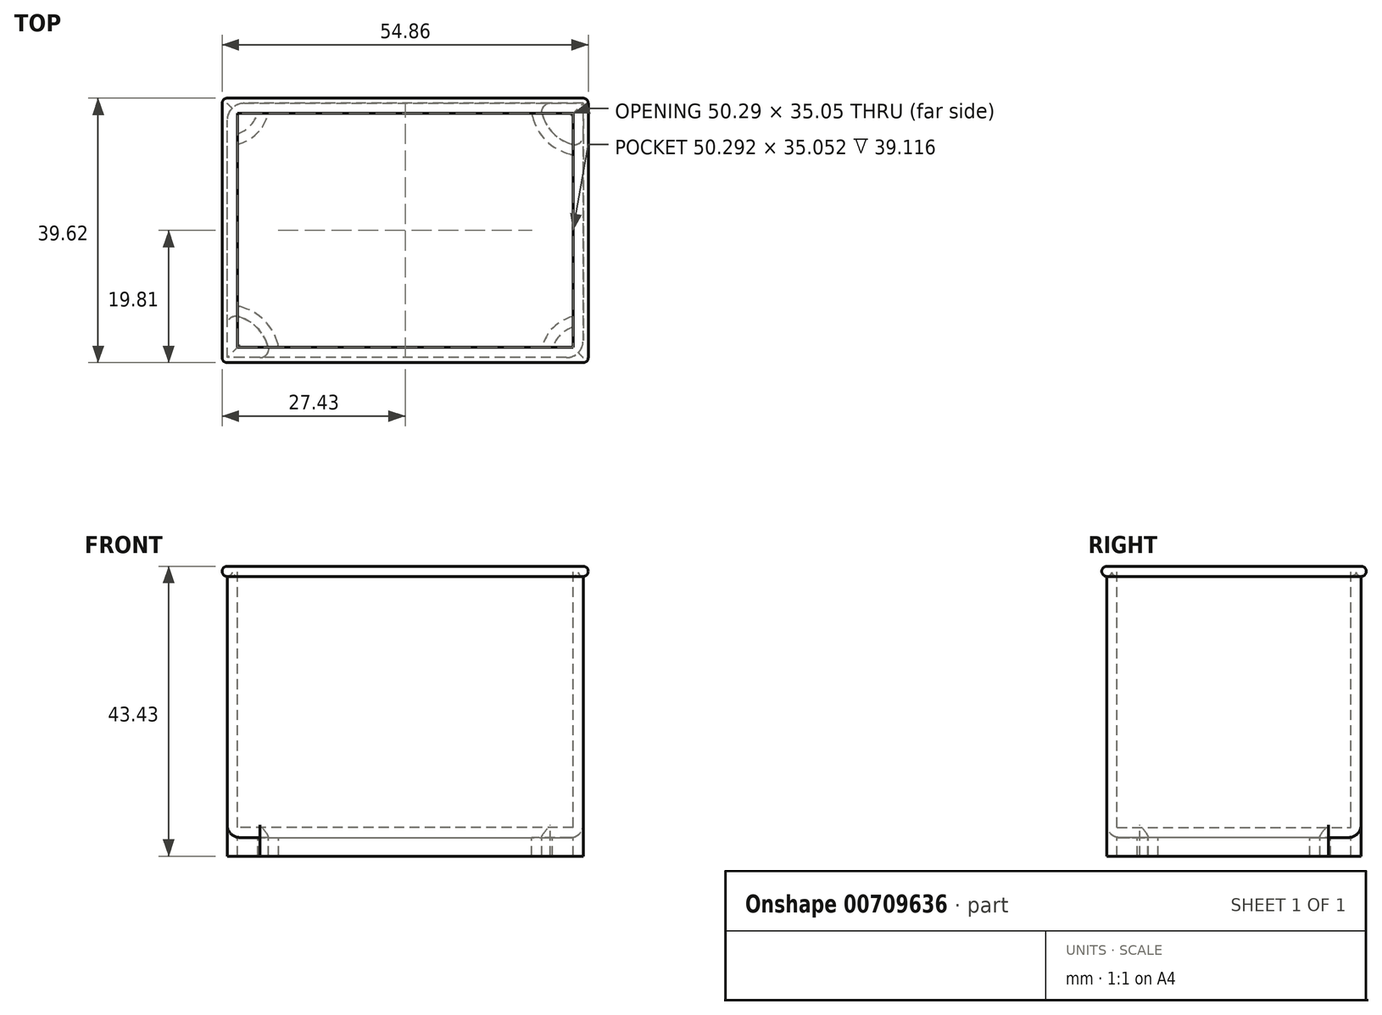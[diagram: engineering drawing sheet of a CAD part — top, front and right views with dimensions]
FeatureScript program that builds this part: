
annotation { "Feature Type Name" : "Feature", "Feature Type Description" : "" }
export const myFeature = defineFeature(function(context is Context, id is Id, definition is map)
    precondition{}
    {
        {
            var Q0;
            Q0=qCreatedBy(makeId("Front.planeOp"),FACE);
            var sketch = newSketch(context, id + "F0", { "sketchPlane" : qUnion([Q0])});
            skLineSegment(sketch, "E0.bottom", {"start": v(26.67, -20.32) * mm, "end": v(-26.67, -20.32) * mm});
            skLineSegment(sketch, "E0.top", {"start": v(26.67, 20.32) * mm, "end": v(-26.67, 20.32) * mm});
            skLineSegment(sketch, "E0.left", {"start": v(26.67, -20.32) * mm, "end": v(26.67, 20.32) * mm});
            skLineSegment(sketch, "E0.right", {"start": v(-26.67, -20.32) * mm, "end": v(-26.67, 20.32) * mm});
            skPoint(sketch, "E0.middle", {"position": v(0, 0) * mm});
            skSolve(sketch);
        }
        {
            var Q0;
            Q0=makeQuery(id+"F0.imprint","IMPRINT",FACE,{"disambiguationData":[TD([[makeQuery(id+"F0.imprint","IMPRINT",EDGE,{"derivedFrom":sQuery(id+"F0.wireOp",EDGE,"E0.bottom")}),-1.0]])]});
            extrude(context, id + "F1", {"entities" : qUnion([Q0]), "depth" : 38.1 * mm, "symmetric" : true});
        }
        {
            var Q0;
            Q0=makeQuery(id+"F1.opExtrude","SWEPT_FACE",FACE,{"disambiguationData":[OSD([sQuery(id+"F0.wireOp",EDGE,"E0.top")])]});
            shell(context, id + "F2", {"entities" : qUnion([Q0]), "thickness" : 1.52 * mm});
        }
        {
            var Q0;
            Q0=makeQuery(id+"F1.opExtrude","CAP_FACE",FACE,{"disambiguationData":[OSD([sQuery(id+"F0.wireOp",EDGE,"E0.bottom"),sQuery(id+"F0.wireOp",EDGE,"E0.top"),sQuery(id+"F0.wireOp",EDGE,"E0.left"),sQuery(id+"F0.wireOp",EDGE,"E0.right")])],"isStart":false});
            var sketch = newSketch(context, id + "F3", { "sketchPlane" : qUnion([Q0])});
            skArc(sketch, "E1", {"start": v(-26.67, 20.32) * mm, "mid": v(-27.43, 19.56) * mm, "end": v(-26.67, 18.8) * mm});
            skSolve(sketch);
        }
        {
            var Q0;
            {var subQ0=sQuery(id+"F3.wireOp",EDGE,"E1");Q0=makeQuery(id+"F3.imprint","IMPRINT",FACE,{"disambiguationData":[TD([[makeQuery(id+"F3.imprint","IMPRINT",EDGE,{"derivedFrom":subQ0}),1.0]])]});}
            var Q1;
            Q1=makeQuery(id+"F1.opExtrude","SWEPT_EDGE",EDGE,{"disambiguationData":[OSD([sQuery(id+"F0.wireOp",EDGE,"E0.top"),sQuery(id+"F0.wireOp",EDGE,"E0.right")])]});
            var Q2;
            Q2=makeQuery(id+"F1.opExtrude","CAP_EDGE",EDGE,{"disambiguationData":[OSD([sQuery(id+"F0.wireOp",EDGE,"E0.top")])],"isStart":true});
            var Q3;
            Q3=makeQuery(id+"F1.opExtrude","SWEPT_EDGE",EDGE,{"disambiguationData":[OSD([sQuery(id+"F0.wireOp",EDGE,"E0.top"),sQuery(id+"F0.wireOp",EDGE,"E0.left")])]});
            var Q4;
            Q4=makeQuery(id+"F1.opExtrude","CAP_EDGE",EDGE,{"disambiguationData":[OSD([sQuery(id+"F0.wireOp",EDGE,"E0.top")])],"isStart":false});
            sweep(context, id + "F4", {"operationType" : NewBodyOperationType.ADD, "profiles" : qUnion([Q0]), "path" : qUnion([Q1, Q2, Q3, Q4])});
        }
        {
            var Q0;
            Q0=makeQuery(id+"F1.opExtrude","SWEPT_FACE",FACE,{"disambiguationData":[OSD([sQuery(id+"F0.wireOp",EDGE,"E0.bottom")])]});
            var sketch = newSketch(context, id + "F5", { "sketchPlane" : qUnion([Q0])});
            skLineSegment(sketch, "E2.bottom", {"start": v(26.67, 19.05) * mm, "end": v(21.75, 19.05) * mm});
            skLineSegment(sketch, "E2.left", {"start": v(26.67, 19.05) * mm, "end": v(26.67, 14.13) * mm});
            skPoint(sketch, "E3.newPointA", {"position": v(20.32, 19.05) * mm});
            skArc(sketch, "E4", {"start": v(20.52, 17.46) * mm, "mid": v(22.18, 14.56) * mm, "end": v(25.08, 12.9) * mm});
            skArc(sketch, "E5.filletArc", {"start": v(21.75, 19.05) * mm, "mid": v(20.75, 18.56) * mm, "end": v(20.52, 17.46) * mm});
            skPoint(sketch, "E6.visualSharp", {"position": v(26.67, 12.7) * mm});
            skArc(sketch, "E6.filletArc", {"start": v(25.08, 12.9) * mm, "mid": v(26.18, 13.13) * mm, "end": v(26.67, 14.13) * mm});
            skArc(sketch, "E7.MirrorCS", {"start": v(-21.75, 19.05) * mm, "mid": v(-20.75, 18.56) * mm, "end": v(-20.52, 17.46) * mm});
            skArc(sketch, "E8.MirrorCS", {"start": v(-20.52, 17.46) * mm, "mid": v(-22.18, 14.56) * mm, "end": v(-25.08, 12.9) * mm});
            skArc(sketch, "E9.MirrorCS", {"start": v(-25.08, 12.9) * mm, "mid": v(-26.18, 13.13) * mm, "end": v(-26.67, 14.13) * mm});
            skLineSegment(sketch, "E10.MirrorCS", {"start": v(-26.67, 19.05) * mm, "end": v(-26.67, 14.13) * mm});
            skLineSegment(sketch, "E11.MirrorCS", {"start": v(-26.67, 19.05) * mm, "end": v(-21.75, 19.05) * mm});
            skArc(sketch, "E12.MirrorCS", {"start": v(-20.52, -17.46) * mm, "mid": v(-22.18, -14.56) * mm, "end": v(-25.08, -12.9) * mm});
            skArc(sketch, "E13.MirrorCS", {"start": v(-21.75, -19.05) * mm, "mid": v(-20.75, -18.56) * mm, "end": v(-20.52, -17.46) * mm});
            skLineSegment(sketch, "E14.MirrorCS", {"start": v(-26.67, -19.05) * mm, "end": v(-21.75, -19.05) * mm});
            skLineSegment(sketch, "E15.MirrorCS", {"start": v(-26.67, -19.05) * mm, "end": v(-26.67, -14.13) * mm});
            skArc(sketch, "E16.MirrorCS", {"start": v(-25.08, -12.9) * mm, "mid": v(-26.18, -13.13) * mm, "end": v(-26.67, -14.13) * mm});
            skArc(sketch, "E17.MirrorCS", {"start": v(21.75, -19.05) * mm, "mid": v(20.75, -18.56) * mm, "end": v(20.52, -17.46) * mm});
            skArc(sketch, "E18.MirrorCS", {"start": v(20.52, -17.46) * mm, "mid": v(22.18, -14.56) * mm, "end": v(25.08, -12.9) * mm});
            skArc(sketch, "E19.MirrorCS", {"start": v(25.08, -12.9) * mm, "mid": v(26.18, -13.13) * mm, "end": v(26.67, -14.13) * mm});
            skLineSegment(sketch, "E20.MirrorCS", {"start": v(26.67, -19.05) * mm, "end": v(26.67, -14.13) * mm});
            skLineSegment(sketch, "E21.MirrorCS", {"start": v(26.67, -19.05) * mm, "end": v(21.75, -19.05) * mm});
            skSolve(sketch);
        }
        {
            var Q0;
            Q0=makeQuery(id+"F5.imprint","IMPRINT",FACE,{"disambiguationData":[TD([[makeQuery(id+"F5.imprint","IMPRINT",EDGE,{"derivedFrom":sQuery(id+"F5.wireOp",EDGE,"E2.bottom")}),1.0]])]});
            var Q1;
            Q1=makeQuery(id+"F5.imprint","IMPRINT",FACE,{"disambiguationData":[TD([[makeQuery(id+"F5.imprint","IMPRINT",EDGE,{"derivedFrom":sQuery(id+"F5.wireOp",EDGE,"E8.MirrorCS")}),-1.0]])]});
            var Q2;
            Q2=makeQuery(id+"F5.imprint","IMPRINT",FACE,{"disambiguationData":[TD([[makeQuery(id+"F5.imprint","IMPRINT",EDGE,{"derivedFrom":sQuery(id+"F5.wireOp",EDGE,"E12.MirrorCS")}),1.0]])]});
            var Q3;
            Q3=makeQuery(id+"F5.imprint","IMPRINT",FACE,{"disambiguationData":[TD([[makeQuery(id+"F5.imprint","IMPRINT",EDGE,{"derivedFrom":sQuery(id+"F5.wireOp",EDGE,"E17.MirrorCS")}),-1.0]])]});
            extrude(context, id + "F6", {"entities" : qUnion([Q0, Q1, Q2, Q3]), "operationType" : NewBodyOperationType.ADD, "depth" : 2.8 * mm});
        }
        {
            var Q0;
            Q0=makeQuery(id+"F6.opExtrude","CAP_FACE",FACE,{"disambiguationData":[OSD([sQuery(id+"F5.wireOp",EDGE,"E2.bottom"),sQuery(id+"F5.wireOp",EDGE,"E2.left"),sQuery(id+"F5.wireOp",EDGE,"E4"),sQuery(id+"F5.wireOp",EDGE,"E5.filletArc"),sQuery(id+"F5.wireOp",EDGE,"E6.filletArc")])],"isStart":false});
            var Q1;
            Q1=makeQuery(id+"F6.opExtrude","CAP_FACE",FACE,{"disambiguationData":[OSD([sQuery(id+"F5.wireOp",EDGE,"E8.MirrorCS"),sQuery(id+"F5.wireOp",EDGE,"E9.MirrorCS"),sQuery(id+"F5.wireOp",EDGE,"E10.MirrorCS"),sQuery(id+"F5.wireOp",EDGE,"E7.MirrorCS"),sQuery(id+"F5.wireOp",EDGE,"E11.MirrorCS")])],"isStart":false});
            var Q2;
            Q2=makeQuery(id+"F6.opExtrude","CAP_FACE",FACE,{"disambiguationData":[OSD([sQuery(id+"F5.wireOp",EDGE,"E12.MirrorCS"),sQuery(id+"F5.wireOp",EDGE,"E13.MirrorCS"),sQuery(id+"F5.wireOp",EDGE,"E14.MirrorCS"),sQuery(id+"F5.wireOp",EDGE,"E15.MirrorCS"),sQuery(id+"F5.wireOp",EDGE,"E16.MirrorCS")])],"isStart":false});
            var Q3;
            Q3=makeQuery(id+"F6.opExtrude","CAP_FACE",FACE,{"disambiguationData":[OSD([sQuery(id+"F5.wireOp",EDGE,"E17.MirrorCS"),sQuery(id+"F5.wireOp",EDGE,"E18.MirrorCS"),sQuery(id+"F5.wireOp",EDGE,"E19.MirrorCS"),sQuery(id+"F5.wireOp",EDGE,"E20.MirrorCS"),sQuery(id+"F5.wireOp",EDGE,"E21.MirrorCS")])],"isStart":false});
            shell(context, id + "F7", {"entities" : qUnion([Q0, Q1, Q2, Q3]), "thickness" : 1.52 * mm});
        }
        {
            var Q0;
            Q0=makeQuery(id+"F1.opExtrude","SWEPT_EDGE",EDGE,{"disambiguationData":[OSD([sQuery(id+"F0.wireOp",EDGE,"E0.bottom"),sQuery(id+"F0.wireOp",EDGE,"E0.right")])]});
            var Q1;
            Q1=makeQuery(id+"F1.opExtrude","CAP_EDGE",EDGE,{"disambiguationData":[OSD([sQuery(id+"F0.wireOp",EDGE,"E0.bottom")])],"isStart":false});
            var Q2;
            Q2=makeQuery(id+"F1.opExtrude","SWEPT_EDGE",EDGE,{"disambiguationData":[OSD([sQuery(id+"F0.wireOp",EDGE,"E0.bottom"),sQuery(id+"F0.wireOp",EDGE,"E0.left")])]});
            var Q3;
            Q3=makeQuery(id+"F1.opExtrude","CAP_EDGE",EDGE,{"disambiguationData":[OSD([sQuery(id+"F0.wireOp",EDGE,"E0.bottom")])],"isStart":true});
            fillet(context, id + "F8", {"entities" : qUnion([Q0, Q1, Q2, Q3]), "radius" : 1.9 * mm, "tangentPropagation" : true, "allowEdgeOverflow" : false});
        }
        {
            var Q0;
            Q0=makeQuery(id+"F4.opSweep","MID_CAP_EDGE",EDGE,{"disambiguationData":[OSD([sQuery(id+"F0.wireOp",EDGE,"E0.top"),sQuery(id+"F0.wireOp",EDGE,"E0.left"),sQuery(id+"F3.wireOp",EDGE,"E1")])],"capPos":3.0});
            var Q1;
            Q1=makeQuery(id+"F4.opSweep","MID_CAP_EDGE",EDGE,{"disambiguationData":[OSD([sQuery(id+"F0.wireOp",EDGE,"E0.top"),sQuery(id+"F0.wireOp",EDGE,"E0.left"),sQuery(id+"F3.wireOp",EDGE,"E1")])],"capPos":2.0});
            var Q2;
            Q2=makeQuery(id+"F4.opSweep","MID_CAP_EDGE",EDGE,{"disambiguationData":[OSD([sQuery(id+"F0.wireOp",EDGE,"E0.top"),sQuery(id+"F0.wireOp",EDGE,"E0.right"),sQuery(id+"F3.wireOp",EDGE,"E1")])],"capPos":1.0});
            var Q3;
            Q3=makeQuery(id+"F4.opSweep","CAP_EDGE",EDGE,{"disambiguationData":[OSD([sQuery(id+"F0.wireOp",EDGE,"E0.top"),sQuery(id+"F0.wireOp",EDGE,"E0.right"),sQuery(id+"F3.wireOp",EDGE,"E1")])],"isStart":true});
            fillet(context, id + "F9", {"entities" : qUnion([Q0, Q1, Q2, Q3]), "radius" : 0.76 * mm, "tangentPropagation" : true, "allowEdgeOverflow" : false});
        }
        {
            var Q0;
            Q0=makeQuery(id+"F6.boolean.opBoolean","MERGE",EDGE,{"derivedFrom":[makeQuery(id+"F1.opExtrude","CAP_EDGE",EDGE,{"disambiguationData":[OSD([sQuery(id+"F0.wireOp",EDGE,"E0.left")])],"isStart":false}),makeQuery(id+"F6.opExtrude","SWEPT_EDGE",EDGE,{"disambiguationData":[OSD([sQuery(id+"F5.wireOp",EDGE,"E2.bottom"),sQuery(id+"F5.wireOp",EDGE,"E2.left")])]})]});
            var Q1;
            Q1=makeQuery(id+"F6.boolean.opBoolean","MERGE",EDGE,{"derivedFrom":[makeQuery(id+"F1.opExtrude","CAP_EDGE",EDGE,{"disambiguationData":[OSD([sQuery(id+"F0.wireOp",EDGE,"E0.left")])],"isStart":true}),makeQuery(id+"F6.opExtrude","SWEPT_EDGE",EDGE,{"disambiguationData":[OSD([sQuery(id+"F5.wireOp",EDGE,"E20.MirrorCS"),sQuery(id+"F5.wireOp",EDGE,"E21.MirrorCS")])]})]});
            var Q2;
            Q2=makeQuery(id+"F6.boolean.opBoolean","MERGE",EDGE,{"derivedFrom":[makeQuery(id+"F1.opExtrude","CAP_EDGE",EDGE,{"disambiguationData":[OSD([sQuery(id+"F0.wireOp",EDGE,"E0.right")])],"isStart":false}),makeQuery(id+"F6.opExtrude","SWEPT_EDGE",EDGE,{"disambiguationData":[OSD([sQuery(id+"F5.wireOp",EDGE,"E10.MirrorCS"),sQuery(id+"F5.wireOp",EDGE,"E11.MirrorCS")])]})]});
            var Q3;
            Q3=makeQuery(id+"F6.boolean.opBoolean","MERGE",EDGE,{"derivedFrom":[makeQuery(id+"F1.opExtrude","CAP_EDGE",EDGE,{"disambiguationData":[OSD([sQuery(id+"F0.wireOp",EDGE,"E0.right")])],"isStart":true}),makeQuery(id+"F6.opExtrude","SWEPT_EDGE",EDGE,{"disambiguationData":[OSD([sQuery(id+"F5.wireOp",EDGE,"E14.MirrorCS"),sQuery(id+"F5.wireOp",EDGE,"E15.MirrorCS")])]})]});
            fillet(context, id + "F10", {"entities" : qUnion([Q0, Q1, Q2, Q3]), "radius" : 2.54 * mm, "tangentPropagation" : true, "allowEdgeOverflow" : false});
        }
    });
